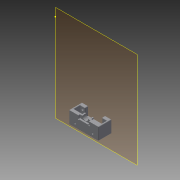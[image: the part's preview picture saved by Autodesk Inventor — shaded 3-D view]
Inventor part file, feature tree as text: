
AUTODESK INVENTOR PART (.ipt)
format: ipt  version: 2014 (Build 180170000, 170)  size: 282,112 bytes
history: native  units: in
note: dims shown in document units (in); Inventor stores cm internally (conversion verified against a paired STEP export)
features: reference x14, sketch x9, extrude x8, plane x3, fillet x1
ambient origin geometry x8: Origin, YZ Plane, XZ Plane, XY Plane, X Axis, Y Axis, Z Axis, Center Point
bodies: Solid1 (feature_tree)
feature tree (35):
  plane  "Work Plane1"
  extrude  "Extrusion1"  Depth=0.1in
  extrude  "Extrusion2"  Depth=0.4528in TaperAngle=0.0deg
  extrude  "Extrusion3"  Depth=0.4724in
  extrude  "Extrusion4"  Depth=0.4724in
  sketch  "Sketch5"  dims[d14=0.1181in d15=0.1181in]
  extrude  "Extrusion5"  Depth=0.1181in
  extrude  "Extrusion6"  Depth=0.6024in TaperAngle=0.0deg
  sketch  "Sketch8"  dims[d22=0.1969in d23=0.1181in d24=0.1181in]
  plane  "Work Plane2"
  extrude  "Extrusion7"  Depth=0.1181in
  sketch  "Sketch9"  dims[d25=6.0in d26=0.0in d28=0.1004in d29=0.0in d30=0.0988in d31=0.0in d32=0.2165in d33=0.2953in d34=0.0988in d35=0.0in d36=0.0394in]
  plane  "Work Plane3"
  extrude  "Extrusion8"  Depth=0.1969in
  fillet  "Fillet2"  Radius=0.1181in
  sketch  "Sketch1"  dims[d2=0.1969in d3=0.0in d4=0.1in]
  reference  "Reference1"
  reference  "Reference2"
  reference  "Reference3"
  reference  "Reference4"
  reference  "Reference5"
  reference  "Reference6"
  reference  "Reference7"
  reference  "Reference8"
  reference  "Reference9"
  reference  "Reference10"
  reference  "Reference11"
  sketch  "Sketch2"  dims[d5=0.1in d6=0.4528in d7=0.0in]
  sketch  "Sketch3"  dims[d10=0.6102in d11=0.4724in]
  reference  "Reference12"
  reference  "Reference13"
  sketch  "Sketch4"  dims[d12=0.6102in d13=0.4724in]
  sketch  "Sketch6"  dims[d16=0.2087in d17=0.0in d18=0.6024in d19=0.0in]
  sketch  "Sketch7"  dims[d20=0.1181in d21=0.1181in]
  reference  "Reference14"
